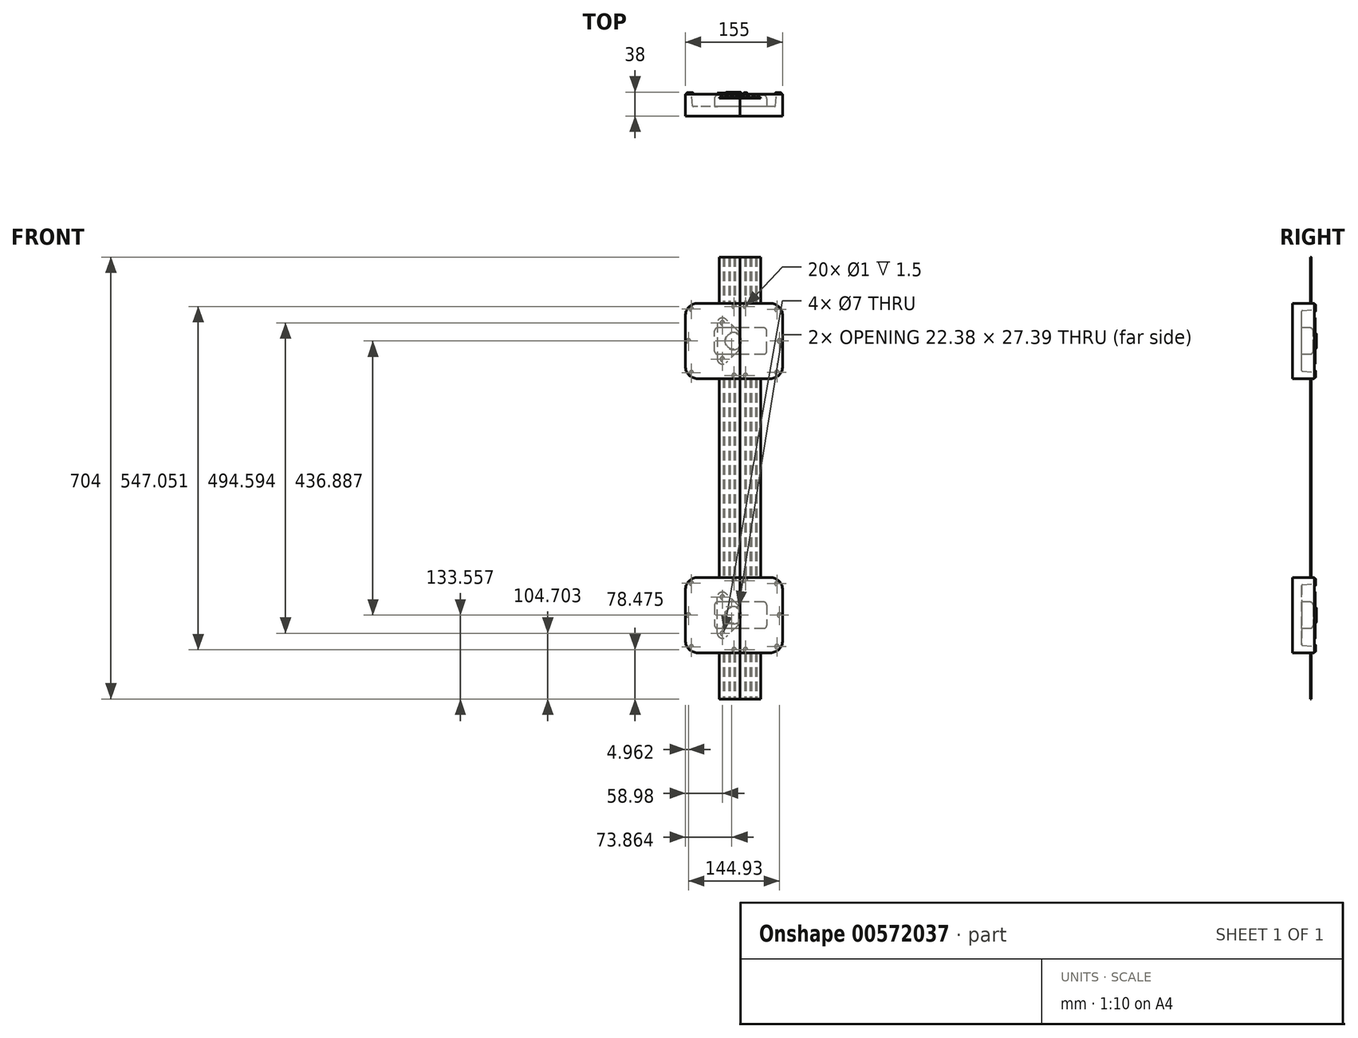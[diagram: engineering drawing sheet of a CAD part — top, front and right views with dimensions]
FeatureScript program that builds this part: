
annotation { "Feature Type Name" : "Feature", "Feature Type Description" : "" }
export const myFeature = defineFeature(function(context is Context, id is Id, definition is map)
    precondition{}
    {
        {
            var Q0;
            Q0=qCreatedBy(makeId("Top.planeOp"),FACE);
            var sketch = newSketch(context, id + "F0", { "sketchPlane" : qUnion([Q0])});
            skLineSegment(sketch, "E0", {"start": v(0, 0) * mm, "end": v(0, 7.5) * mm});
            skPoint(sketch, "E1.visualSharp", {"position": v(0, 36) * mm});
            skArc(sketch, "E1.filletArc", {"start": v(0.59, 35.41) * mm, "mid": v(0.15, 34.77) * mm, "end": v(0, 34) * mm});
            skLineSegment(sketch, "E2.1", {"start": v(1.5, 0) * mm, "end": v(1.5, 33.5) * mm});
            skLineSegment(sketch, "E3", {"start": v(1.5, 0) * mm, "end": v(0, 0) * mm});
            skPoint(sketch, "E4.visualSharp", {"position": v(1.5, 34.5) * mm});
            skArc(sketch, "E4.filletArc", {"start": v(1.8, 34.2) * mm, "mid": v(1.58, 33.88) * mm, "end": v(1.5, 33.5) * mm});
            skLineSegment(sketch, "E5.bottom", {"start": v(0, 18) * mm, "end": v(0.25, 18) * mm});
            skLineSegment(sketch, "E5.top", {"start": v(0, 16) * mm, "end": v(0.25, 16) * mm});
            skLineSegment(sketch, "E5.right", {"start": v(0.25, 18) * mm, "end": v(0.25, 16) * mm});
            skPoint(sketch, "E5.middle", {"position": v(0, 17) * mm});
            skLineSegment(sketch, "E6", {"start": v(0, 0) * mm, "end": v(-1.84, 0) * mm, "construction": true});
            skLineSegment(sketch, "E7", {"start": v(-1.84, 0) * mm, "end": v(-1.84, 17) * mm, "construction": true});
            skPoint(sketch, "E7.endSnap0", {"position": v(-0.25, 17) * mm});
            skLineSegment(sketch, "E8", {"start": v(-1.84, 8.5) * mm, "end": v(0, 8.5) * mm, "construction": true});
            skLineSegment(sketch, "E9.bottom", {"start": v(0.25, 9.5) * mm, "end": v(0, 9.5) * mm});
            skLineSegment(sketch, "E9.top", {"start": v(0.25, 7.5) * mm, "end": v(0, 7.5) * mm});
            skLineSegment(sketch, "E9.left", {"start": v(0.25, 9.5) * mm, "end": v(0.25, 7.5) * mm});
            skPoint(sketch, "E9.middle", {"position": v(0, 8.5) * mm});
            skLineSegment(sketch, "E10", {"start": v(-1.84, 17) * mm, "end": v(-1.84, 34) * mm, "construction": true});
            skLineSegment(sketch, "E11", {"start": v(-1.84, 25.5) * mm, "end": v(0, 25.5) * mm, "construction": true});
            skLineSegment(sketch, "E12.bottom", {"start": v(0.25, 26.5) * mm, "end": v(0, 26.5) * mm});
            skLineSegment(sketch, "E12.top", {"start": v(0.25, 24.5) * mm, "end": v(0, 24.5) * mm});
            skLineSegment(sketch, "E12.left", {"start": v(0.25, 26.5) * mm, "end": v(0.25, 24.5) * mm});
            skPoint(sketch, "E12.middle", {"position": v(0, 25.5) * mm});
            skPoint(sketch, "E13.end.orphan", {"position": v(36, 36) * mm});
            skLineSegment(sketch, "E14.trimOffspring", {"start": v(0, 9.5) * mm, "end": v(0, 16) * mm});
            skPoint(sketch, "E15.orphan", {"position": v(-0.25, 9.5) * mm});
            skPoint(sketch, "E16.orphan", {"position": v(-0.25, 7.5) * mm});
            skPoint(sketch, "E17.orphan", {"position": v(-0.25, 16) * mm});
            skLineSegment(sketch, "E18.trimOffspring", {"start": v(0, 18) * mm, "end": v(0, 24.5) * mm});
            skPoint(sketch, "E19.orphan", {"position": v(-0.25, 18) * mm});
            skLineSegment(sketch, "E20.trimOffspring", {"start": v(0, 26.5) * mm, "end": v(0, 34) * mm});
            skPoint(sketch, "E21.orphan", {"position": v(-0.25, 24.5) * mm});
            skPoint(sketch, "E22.orphan", {"position": v(-0.25, 26.5) * mm});
            skLineSegment(sketch, "E23.MirrorCS", {"start": v(11.5, 35.75) * mm, "end": v(11.5, 36) * mm});
            skLineSegment(sketch, "E24.MirrorCS", {"start": v(26.5, 35.75) * mm, "end": v(28.5, 35.75) * mm});
            skLineSegment(sketch, "E25.MirrorCS", {"start": v(28.5, 35.75) * mm, "end": v(28.5, 36) * mm});
            skLineSegment(sketch, "E26.MirrorCS", {"start": v(9.5, 35.75) * mm, "end": v(11.5, 35.75) * mm});
            skLineSegment(sketch, "E27.MirrorCS", {"start": v(9.5, 35.75) * mm, "end": v(9.5, 36) * mm});
            skLineSegment(sketch, "E28.MirrorCS", {"start": v(20, 36) * mm, "end": v(20, 35.75) * mm});
            skLineSegment(sketch, "E29.MirrorCS", {"start": v(26.5, 35.75) * mm, "end": v(26.5, 36) * mm});
            skLineSegment(sketch, "E30.MirrorCS", {"start": v(18, 35.75) * mm, "end": v(20, 35.75) * mm});
            skLineSegment(sketch, "E31.MirrorCS", {"start": v(18, 36) * mm, "end": v(18, 35.75) * mm});
            skArc(sketch, "E32.MirrorCS", {"start": v(1.8, 34.2) * mm, "mid": v(2.12, 34.42) * mm, "end": v(2.5, 34.5) * mm});
            skLineSegment(sketch, "E33.MirrorCS", {"start": v(36, 34.5) * mm, "end": v(36, 36) * mm});
            skArc(sketch, "E34.MirrorCS", {"start": v(0.59, 35.41) * mm, "mid": v(1.23, 35.85) * mm, "end": v(2, 36) * mm});
            skLineSegment(sketch, "E35.MirrorCS", {"start": v(10.5, 37.84) * mm, "end": v(10.5, 36) * mm, "construction": true});
            skLineSegment(sketch, "E36.MirrorCS", {"start": v(36, 36) * mm, "end": v(36, 37.84) * mm, "construction": true});
            skPoint(sketch, "E37.MirrorP", {"position": v(19, 36.25) * mm});
            skLineSegment(sketch, "E38.MirrorCS", {"start": v(27.5, 37.84) * mm, "end": v(27.5, 36) * mm, "construction": true});
            skPoint(sketch, "E39.MirrorP", {"position": v(19, 36) * mm});
            skLineSegment(sketch, "E40.MirrorCS", {"start": v(36, 34.5) * mm, "end": v(2.5, 34.5) * mm});
            skPoint(sketch, "E41.MirrorP", {"position": v(27.5, 36) * mm});
            skLineSegment(sketch, "E42.MirrorCS", {"start": v(36, 36) * mm, "end": v(28.5, 36) * mm});
            skLineSegment(sketch, "E43.MirrorCS", {"start": v(19, 37.84) * mm, "end": v(2, 37.84) * mm, "construction": true});
            skPoint(sketch, "E44.MirrorP", {"position": v(28.5, 36.25) * mm});
            skLineSegment(sketch, "E45.MirrorCS", {"start": v(18, 36) * mm, "end": v(11.5, 36) * mm});
            skPoint(sketch, "E46.MirrorP", {"position": v(18, 36.25) * mm});
            skPoint(sketch, "E47.MirrorP", {"position": v(10.5, 36) * mm});
            skPoint(sketch, "E48.MirrorP", {"position": v(9.5, 36.25) * mm});
            skPoint(sketch, "E49.MirrorP", {"position": v(20, 36.25) * mm});
            skPoint(sketch, "E50.MirrorP", {"position": v(26.5, 36.25) * mm});
            skLineSegment(sketch, "E51.MirrorCS", {"start": v(9.5, 36) * mm, "end": v(2, 36) * mm});
            skLineSegment(sketch, "E52.MirrorCS", {"start": v(36, 37.84) * mm, "end": v(19, 37.84) * mm, "construction": true});
            skPoint(sketch, "E53.MirrorP", {"position": v(11.5, 36.25) * mm});
            skLineSegment(sketch, "E54.MirrorCS", {"start": v(26.5, 36) * mm, "end": v(20, 36) * mm});
            skSolve(sketch);
        }
        {
            var Q0;
            Q0=qSketchRegion(id+"F0",true);
            extrude(context, id + "F1", {"entities" : qUnion([Q0]), "depth" : 704 * mm, "offsetDistance" : 25 * mm});
        }
        {
            var Q0;
            Q0=makeQuery(id+"F1.opExtrude","CAP_FACE",FACE,{"disambiguationData":[OSD([sQuery(id+"F0.wireOp",EDGE,"E0"),sQuery(id+"F0.wireOp",EDGE,"E1.filletArc"),sQuery(id+"F0.wireOp",EDGE,"E2.1"),sQuery(id+"F0.wireOp",EDGE,"E3"),sQuery(id+"F0.wireOp",EDGE,"E4.filletArc"),sQuery(id+"F0.wireOp",EDGE,"E5.bottom"),sQuery(id+"F0.wireOp",EDGE,"E5.top"),sQuery(id+"F0.wireOp",EDGE,"E5.right"),sQuery(id+"F0.wireOp",EDGE,"E9.bottom"),sQuery(id+"F0.wireOp",EDGE,"E9.top"),sQuery(id+"F0.wireOp",EDGE,"E9.left"),sQuery(id+"F0.wireOp",EDGE,"E12.bottom"),sQuery(id+"F0.wireOp",EDGE,"E12.top"),sQuery(id+"F0.wireOp",EDGE,"E12.left"),sQuery(id+"F0.wireOp",EDGE,"E14.trimOffspring"),sQuery(id+"F0.wireOp",EDGE,"E18.trimOffspring"),sQuery(id+"F0.wireOp",EDGE,"E20.trimOffspring"),sQuery(id+"F0.wireOp",EDGE,"E23.MirrorCS"),sQuery(id+"F0.wireOp",EDGE,"E24.MirrorCS"),sQuery(id+"F0.wireOp",EDGE,"E25.MirrorCS"),sQuery(id+"F0.wireOp",EDGE,"E26.MirrorCS"),sQuery(id+"F0.wireOp",EDGE,"E27.MirrorCS"),sQuery(id+"F0.wireOp",EDGE,"E28.MirrorCS"),sQuery(id+"F0.wireOp",EDGE,"E29.MirrorCS"),sQuery(id+"F0.wireOp",EDGE,"E30.MirrorCS"),sQuery(id+"F0.wireOp",EDGE,"E31.MirrorCS"),sQuery(id+"F0.wireOp",EDGE,"E32.MirrorCS"),sQuery(id+"F0.wireOp",EDGE,"E33.MirrorCS"),sQuery(id+"F0.wireOp",EDGE,"E34.MirrorCS"),sQuery(id+"F0.wireOp",EDGE,"E40.MirrorCS"),sQuery(id+"F0.wireOp",EDGE,"E42.MirrorCS"),sQuery(id+"F0.wireOp",EDGE,"E45.MirrorCS"),sQuery(id+"F0.wireOp",EDGE,"E51.MirrorCS"),sQuery(id+"F0.wireOp",EDGE,"E54.MirrorCS")])],"isStart":false});
            var sketch = newSketch(context, id + "F2", { "sketchPlane" : qUnion([Q0])});
            skLineSegment(sketch, "E55.bottom", {"start": v(0, 0) * mm, "end": v(3, 0) * mm});
            skLineSegment(sketch, "E55.top", {"start": v(0, 37.06) * mm, "end": v(3, 37.06) * mm});
            skLineSegment(sketch, "E55.left", {"start": v(0, 0) * mm, "end": v(0, 37.06) * mm});
            skLineSegment(sketch, "E55.right", {"start": v(3, 0) * mm, "end": v(3, 37.06) * mm});
            skSolve(sketch);
        }
        {
            var Q0;
            {var subQ4=sQuery(id+"F2.wireOp",EDGE,"E55.top");Q0=makeQuery(id+"F2.imprint","IMPRINT",FACE,{"disambiguationData":[TD([[makeQuery(id+"F2.imprint","IMPRINT",EDGE,{"derivedFrom":subQ4}),-1.0]])]});}
            var Q1;
            {var subQ4=sQuery(id+"F0.wireOp",EDGE,"E2.1");Q1=makeQuery(id+"F2.imprint","IMPRINT",FACE,{"disambiguationData":[TD([[makeQuery(id+"F2.imprint","IMPRINT",EDGE,{"derivedFrom":makeQuery(id+"F1.opExtrude","CAP_EDGE",EDGE,{"disambiguationData":[OSD([subQ4])],"isStart":false})}),-1.0]])]});}
            var Q2;
            {var subQ13=sQuery(id+"F0.wireOp",EDGE,"E5.right");Q2=makeQuery(id+"F2.imprint","IMPRINT",FACE,{"disambiguationData":[TD([[makeQuery(id+"F2.imprint","IMPRINT",EDGE,{"derivedFrom":makeQuery(id+"F1.opExtrude","CAP_EDGE",EDGE,{"disambiguationData":[OSD([subQ13])],"isStart":false})}),1.0]])]});}
            extrude(context, id + "F3", {"entities" : qUnion([Q0, Q1, Q2]), "operationType" : NewBodyOperationType.REMOVE, "endBound" : BoundingType.THROUGH_ALL, "oppositeDirection" : true, "depth" : 25 * mm, "offsetDistance" : 25 * mm});
        }
        {
            var Q0;
            Q0=makeQuery(id+"F3.boolean.opBoolean","INTERSECT",EDGE,{"derivedFrom":[makeQuery(id+"F1.opExtrude","SWEPT_FACE",FACE,{"disambiguationData":[OSD([sQuery(id+"F0.wireOp",EDGE,"E51.MirrorCS")])]}),makeQuery(id+"F3.opExtrude","SWEPT_FACE",FACE,{"disambiguationData":[OSD([sQuery(id+"F2.wireOp",EDGE,"E55.right")])]})]});
            var Q1;
            Q1=makeQuery(id+"F1.opExtrude","SWEPT_EDGE",EDGE,{"disambiguationData":[OSD([sQuery(id+"F0.wireOp",EDGE,"E33.MirrorCS"),sQuery(id+"F0.wireOp",EDGE,"E42.MirrorCS")])]});
            fillet(context, id + "F4", {"entities" : qUnion([Q0, Q1]), "radius" : 2 * mm, "tangentPropagation" : true, "allowEdgeOverflow" : false});
        }
        {
            var Q0;
            Q0=makeQuery(id+"F1.opExtrude","SWEPT_EDGE",EDGE,{"disambiguationData":[OSD([sQuery(id+"F0.wireOp",EDGE,"E31.MirrorCS"),sQuery(id+"F0.wireOp",EDGE,"E45.MirrorCS")])]});
            var Q1;
            Q1=makeQuery(id+"F1.opExtrude","SWEPT_EDGE",EDGE,{"disambiguationData":[OSD([sQuery(id+"F0.wireOp",EDGE,"E28.MirrorCS"),sQuery(id+"F0.wireOp",EDGE,"E54.MirrorCS")])]});
            var Q2;
            Q2=makeQuery(id+"F1.opExtrude","SWEPT_EDGE",EDGE,{"disambiguationData":[OSD([sQuery(id+"F0.wireOp",EDGE,"E25.MirrorCS"),sQuery(id+"F0.wireOp",EDGE,"E42.MirrorCS")])]});
            var Q3;
            Q3=makeQuery(id+"F1.opExtrude","SWEPT_EDGE",EDGE,{"disambiguationData":[OSD([sQuery(id+"F0.wireOp",EDGE,"E29.MirrorCS"),sQuery(id+"F0.wireOp",EDGE,"E54.MirrorCS")])]});
            var Q4;
            Q4=makeQuery(id+"F1.opExtrude","SWEPT_EDGE",EDGE,{"disambiguationData":[OSD([sQuery(id+"F0.wireOp",EDGE,"E27.MirrorCS"),sQuery(id+"F0.wireOp",EDGE,"E51.MirrorCS")])]});
            var Q5;
            Q5=makeQuery(id+"F1.opExtrude","SWEPT_EDGE",EDGE,{"disambiguationData":[OSD([sQuery(id+"F0.wireOp",EDGE,"E23.MirrorCS"),sQuery(id+"F0.wireOp",EDGE,"E45.MirrorCS")])]});
            fillet(context, id + "F5", {"entities" : qUnion([Q0, Q1, Q2, Q3, Q4, Q5]), "radius" : 0.2 * mm, "tangentPropagation" : true, "allowEdgeOverflow" : false});
        }
        {
            var Q0;
            Q0=qCreatedBy(makeId("Right.planeOp"),FACE);
            cPlane(context, id + "F6", {"entities" : qUnion([Q0]), "cplaneType" : CPlaneType.OFFSET, "offset" : 36.1 * mm, "width" : 150 * mm, "height" : 150 * mm});
        }
        {
            var Q0;
            Q0=makeQuery(id+"F1.opExtrude","SWEPT_BODY",BODY,{"disambiguationData":[OSD([sQuery(id+"F0.wireOp",EDGE,"E0"),sQuery(id+"F0.wireOp",EDGE,"E1.filletArc"),sQuery(id+"F0.wireOp",EDGE,"E2.1"),sQuery(id+"F0.wireOp",EDGE,"E3"),sQuery(id+"F0.wireOp",EDGE,"E4.filletArc"),sQuery(id+"F0.wireOp",EDGE,"E5.bottom"),sQuery(id+"F0.wireOp",EDGE,"E5.top"),sQuery(id+"F0.wireOp",EDGE,"E5.right"),sQuery(id+"F0.wireOp",EDGE,"E9.bottom"),sQuery(id+"F0.wireOp",EDGE,"E9.top"),sQuery(id+"F0.wireOp",EDGE,"E9.left"),sQuery(id+"F0.wireOp",EDGE,"E12.bottom"),sQuery(id+"F0.wireOp",EDGE,"E12.top"),sQuery(id+"F0.wireOp",EDGE,"E12.left"),sQuery(id+"F0.wireOp",EDGE,"E14.trimOffspring"),sQuery(id+"F0.wireOp",EDGE,"E18.trimOffspring"),sQuery(id+"F0.wireOp",EDGE,"E20.trimOffspring"),sQuery(id+"F0.wireOp",EDGE,"E23.MirrorCS"),sQuery(id+"F0.wireOp",EDGE,"E24.MirrorCS"),sQuery(id+"F0.wireOp",EDGE,"E25.MirrorCS"),sQuery(id+"F0.wireOp",EDGE,"E26.MirrorCS"),sQuery(id+"F0.wireOp",EDGE,"E27.MirrorCS"),sQuery(id+"F0.wireOp",EDGE,"E28.MirrorCS"),sQuery(id+"F0.wireOp",EDGE,"E29.MirrorCS"),sQuery(id+"F0.wireOp",EDGE,"E30.MirrorCS"),sQuery(id+"F0.wireOp",EDGE,"E31.MirrorCS"),sQuery(id+"F0.wireOp",EDGE,"E32.MirrorCS"),sQuery(id+"F0.wireOp",EDGE,"E33.MirrorCS"),sQuery(id+"F0.wireOp",EDGE,"E34.MirrorCS"),sQuery(id+"F0.wireOp",EDGE,"E40.MirrorCS"),sQuery(id+"F0.wireOp",EDGE,"E42.MirrorCS"),sQuery(id+"F0.wireOp",EDGE,"E45.MirrorCS"),sQuery(id+"F0.wireOp",EDGE,"E51.MirrorCS"),sQuery(id+"F0.wireOp",EDGE,"E54.MirrorCS")])]});
            var Q1;
            Q1=qCreatedBy(id+"F6.planeOp",FACE);
            mirror(context, id + "F7", {"operationType" : NewBodyOperationType.ADD, "entities" : qUnion([Q0]), "mirrorPlane" : qUnion([Q1])});
        }
        {
            var Q0;
            Q0=makeQuery(id+"F7.opPattern","COPY",FACE,{"derivedFrom":makeQuery(id+"F1.opExtrude","SWEPT_FACE",FACE,{"disambiguationData":[OSD([sQuery(id+"F0.wireOp",EDGE,"E42.MirrorCS")])]}),"instanceName":"1"});
            var sketch = newSketch(context, id + "F8", { "sketchPlane" : qUnion([Q0])});
            skLineSegment(sketch, "E56.bottom", {"start": v(-94.76, 73.56) * mm, "end": v(55.24, 73.56) * mm});
            skLineSegment(sketch, "E56.top", {"start": v(-94.76, 193.56) * mm, "end": v(55.24, 193.56) * mm});
            skLineSegment(sketch, "E56.left", {"start": v(-94.76, 73.56) * mm, "end": v(-94.76, 193.56) * mm});
            skLineSegment(sketch, "E56.right", {"start": v(55.24, 73.56) * mm, "end": v(55.24, 193.56) * mm});
            skPoint(sketch, "E56.middle", {"position": v(-19.76, 133.56) * mm});
            skLineSegment(sketch, "E57", {"start": v(32.68, 352) * mm, "end": v(-137.04, 352) * mm, "construction": true});
            skPoint(sketch, "E57.startSnap0", {"position": v(-43.5, 352) * mm});
            skLineSegment(sketch, "E58.MirrorCS", {"start": v(-94.76, 510.44) * mm, "end": v(55.24, 510.44) * mm});
            skPoint(sketch, "E59.MirrorP", {"position": v(-19.76, 570.44) * mm});
            skLineSegment(sketch, "E60.MirrorCS", {"start": v(-94.76, 630.44) * mm, "end": v(55.24, 630.44) * mm});
            skLineSegment(sketch, "E61.MirrorCS", {"start": v(-94.76, 630.44) * mm, "end": v(-94.76, 510.44) * mm});
            skLineSegment(sketch, "E62.MirrorCS", {"start": v(55.24, 630.44) * mm, "end": v(55.24, 510.44) * mm});
            skSolve(sketch);
        }
        {
            var Q0;
            Q0 = qSketchRegion(id + "F8", true);
            extrude(context, id + "F9", {"entities" : qUnion([Q0]), "operationType" : NewBodyOperationType.REMOVE, "oppositeDirection" : true, "depth" : 25 * mm, "offsetDistance" : 25 * mm, "hasSecondDirection" : true, "secondDirectionOppositeDirection" : false, "secondDirectionDepth" : 25 * mm});
        }
        {
            var Q0;
            {var subQ0=sQuery(id+"F0.wireOp",EDGE,"E51.MirrorCS");Q0=makeQuery(id+"F9.boolean.opBoolean","SPLIT",FACE,{"disambiguationData":[TD([makeQuery(id+"F9.opExtrude","SWEPT_FACE",FACE,{"disambiguationData":[OSD([sQuery(id+"F8.wireOp",EDGE,"E56.bottom")])]})])],"derivedFrom":makeQuery(id+"F7.opPattern","COPY",FACE,{"derivedFrom":makeQuery(id+"F1.opExtrude","SWEPT_FACE",FACE,{"disambiguationData":[OSD([subQ0])]}),"instanceName":"1"})});}
            var sketch = newSketch(context, id + "F10", { "sketchPlane" : qUnion([Q0])});
            skLineSegment(sketch, "E63.bottom", {"start": v(-84.02, 73.56) * mm, "end": v(30.98, 73.56) * mm});
            skLineSegment(sketch, "E63.top", {"start": v(-84.02, 193.56) * mm, "end": v(30.98, 193.56) * mm});
            skLineSegment(sketch, "E63.left", {"start": v(-104.02, 93.56) * mm, "end": v(-104.02, 173.56) * mm});
            skLineSegment(sketch, "E63.right", {"start": v(50.98, 93.56) * mm, "end": v(50.98, 173.56) * mm});
            skPoint(sketch, "E64.visualSharp", {"position": v(-104.02, 73.56) * mm});
            skArc(sketch, "E64.filletArc", {"start": v(-104.02, 93.56) * mm, "mid": v(-98.16, 79.41) * mm, "end": v(-84.02, 73.56) * mm});
            skPoint(sketch, "E65.visualSharp", {"position": v(-104.02, 193.56) * mm});
            skArc(sketch, "E65.filletArc", {"start": v(-84.02, 193.56) * mm, "mid": v(-98.16, 187.7) * mm, "end": v(-104.02, 173.56) * mm});
            skPoint(sketch, "E66.visualSharp", {"position": v(50.98, 193.56) * mm});
            skArc(sketch, "E66.filletArc", {"start": v(50.98, 173.56) * mm, "mid": v(45.13, 187.7) * mm, "end": v(30.98, 193.56) * mm});
            skPoint(sketch, "E67.visualSharp", {"position": v(50.98, 73.56) * mm});
            skArc(sketch, "E67.filletArc", {"start": v(30.98, 73.56) * mm, "mid": v(45.13, 79.41) * mm, "end": v(50.98, 93.56) * mm});
            skSolve(sketch);
        }
        {
            var Q0;
            Q0 = qSketchRegion(id + "F10", true);
            extrude(context, id + "F11", {"entities" : qUnion([Q0]), "depth" : 5 * mm, "offsetDistance" : 25 * mm, "hasSecondDirection" : true, "secondDirectionOppositeDirection" : true, "secondDirectionDepth" : 30 * mm});
        }
        {
            var Q0;
            Q0=makeQuery(id+"F11.opExtrude","CAP_FACE",FACE,{"disambiguationData":[OSD([sQuery(id+"F10.wireOp",EDGE,"E63.bottom"),sQuery(id+"F10.wireOp",EDGE,"E63.top"),sQuery(id+"F10.wireOp",EDGE,"E63.left"),sQuery(id+"F10.wireOp",EDGE,"E63.right"),sQuery(id+"F10.wireOp",EDGE,"E64.filletArc"),sQuery(id+"F10.wireOp",EDGE,"E65.filletArc"),sQuery(id+"F10.wireOp",EDGE,"E66.filletArc"),sQuery(id+"F10.wireOp",EDGE,"E67.filletArc")])],"isStart":false});
            var sketch = newSketch(context, id + "F12", { "sketchPlane" : qUnion([Q0])});
            skLineSegment(sketch, "E68.0", {"start": v(-94.02, 173.56) * mm, "end": v(-94.02, 93.56) * mm});
            skArc(sketch, "E68.1", {"start": v(-84.02, 183.56) * mm, "mid": v(-91.09, 180.63) * mm, "end": v(-94.02, 173.56) * mm});
            skArc(sketch, "E68.2", {"start": v(-94.02, 93.56) * mm, "mid": v(-91.09, 86.49) * mm, "end": v(-84.02, 83.56) * mm});
            skLineSegment(sketch, "E68.3", {"start": v(30.98, 183.56) * mm, "end": v(-84.02, 183.56) * mm});
            skLineSegment(sketch, "E68.4", {"start": v(-84.02, 83.56) * mm, "end": v(30.98, 83.56) * mm});
            skArc(sketch, "E68.5", {"start": v(30.98, 83.56) * mm, "mid": v(38.05, 86.49) * mm, "end": v(40.98, 93.56) * mm});
            skLineSegment(sketch, "E68.6", {"start": v(40.98, 93.56) * mm, "end": v(40.98, 173.56) * mm});
            skArc(sketch, "E68.7", {"start": v(40.98, 173.56) * mm, "mid": v(38.05, 180.63) * mm, "end": v(30.98, 183.56) * mm});
            skSolve(sketch);
        }
        {
            var Q0;
            Q0 = qSketchRegion(id + "F12", true);
            extrude(context, id + "F13", {"entities" : qUnion([Q0]), "operationType" : NewBodyOperationType.REMOVE, "oppositeDirection" : true, "depth" : 20 * mm, "offsetDistance" : 25 * mm, "hasDraft" : true, "draftAngle" : 5 * degree, "draftPullDirection" : true});
        }
        {
            var Q0;
            Q0=makeQuery(id+"F11.opExtrude","CAP_FACE",FACE,{"disambiguationData":[OSD([sQuery(id+"F10.wireOp",EDGE,"E63.bottom"),sQuery(id+"F10.wireOp",EDGE,"E63.top"),sQuery(id+"F10.wireOp",EDGE,"E63.left"),sQuery(id+"F10.wireOp",EDGE,"E63.right"),sQuery(id+"F10.wireOp",EDGE,"E64.filletArc"),sQuery(id+"F10.wireOp",EDGE,"E65.filletArc"),sQuery(id+"F10.wireOp",EDGE,"E66.filletArc"),sQuery(id+"F10.wireOp",EDGE,"E67.filletArc")])],"isStart":false});
            var Q1;
            Q1=makeQuery(id+"F13.boolean.opBoolean","COPY",FACE,{"derivedFrom":makeQuery(id+"F13.opExtrude","CAP_FACE",FACE,{"disambiguationData":[OSD([sQuery(id+"F12.wireOp",EDGE,"E68.0"),sQuery(id+"F12.wireOp",EDGE,"E68.1"),sQuery(id+"F12.wireOp",EDGE,"E68.2"),sQuery(id+"F12.wireOp",EDGE,"E68.3"),sQuery(id+"F12.wireOp",EDGE,"E68.4"),sQuery(id+"F12.wireOp",EDGE,"E68.5"),sQuery(id+"F12.wireOp",EDGE,"E68.6"),sQuery(id+"F12.wireOp",EDGE,"E68.7")])],"isStart":false})});
            fillet(context, id + "F14", {"entities" : qUnion([Q0, Q1]), "radius" : 1 * mm, "tangentPropagation" : true, "allowEdgeOverflow" : false});
        }
        {
            var Q0;
            Q0=makeQuery(id+"F11.opExtrude","CAP_FACE",FACE,{"disambiguationData":[OSD([sQuery(id+"F10.wireOp",EDGE,"E63.bottom"),sQuery(id+"F10.wireOp",EDGE,"E63.top"),sQuery(id+"F10.wireOp",EDGE,"E63.left"),sQuery(id+"F10.wireOp",EDGE,"E63.right"),sQuery(id+"F10.wireOp",EDGE,"E64.filletArc"),sQuery(id+"F10.wireOp",EDGE,"E65.filletArc"),sQuery(id+"F10.wireOp",EDGE,"E66.filletArc"),sQuery(id+"F10.wireOp",EDGE,"E67.filletArc")])],"isStart":false});
            var sketch = newSketch(context, id + "F15", { "sketchPlane" : qUnion([Q0])});
            skCircle(sketch, "E69", {"center": v(-98.91, 133.56) * mm, "radius": 3.5 * mm});
            skCircle(sketch, "E70", {"center": v(-98.91, 133.56) * mm, "radius": 0.5 * mm});
            skCircle(sketch, "E71", {"center": v(-94.92, 83.43) * mm, "radius": 3.5 * mm});
            skCircle(sketch, "E72", {"center": v(-94.92, 83.43) * mm, "radius": 0.5 * mm});
            skCircle(sketch, "E73", {"center": v(-44.7, 78.47) * mm, "radius": 3.5 * mm});
            skCircle(sketch, "E74", {"center": v(-44.7, 78.47) * mm, "radius": 0.5 * mm});
            skCircle(sketch, "E75", {"center": v(46.02, 133.56) * mm, "radius": 3.5 * mm});
            skCircle(sketch, "E76", {"center": v(46.02, 133.56) * mm, "radius": 0.5 * mm});
            skCircle(sketch, "E77", {"center": v(41.31, 82.78) * mm, "radius": 3.5 * mm});
            skCircle(sketch, "E78", {"center": v(41.31, 82.78) * mm, "radius": 0.5 * mm});
            skCircle(sketch, "E79", {"center": v(-26.6, 78.55) * mm, "radius": 3.5 * mm});
            skCircle(sketch, "E80", {"center": v(-26.6, 78.55) * mm, "radius": 0.5 * mm});
            skLineSegment(sketch, "E81", {"start": v(139.82, 74.56) * mm, "end": v(139.82, 192.56) * mm, "construction": true});
            skLineSegment(sketch, "E82", {"start": v(-84.02, 74.56) * mm, "end": v(-84.02, 192.56) * mm, "construction": true});
            skLineSegment(sketch, "E83", {"start": v(-84.02, 133.56) * mm, "end": v(-101.6, 133.56) * mm, "construction": true});
            skPoint(sketch, "E83.endSnap0", {"position": v(-84.02, 133.56) * mm});
            skLineSegment(sketch, "E84", {"start": v(-84.02, 133.56) * mm, "end": v(54.57, 133.56) * mm, "construction": true});
            skCircle(sketch, "E85.MirrorC", {"center": v(-94.92, 183.68) * mm, "radius": 0.5 * mm});
            skCircle(sketch, "E86.MirrorC", {"center": v(-44.7, 188.64) * mm, "radius": 0.5 * mm});
            skCircle(sketch, "E87.MirrorC", {"center": v(-26.6, 188.56) * mm, "radius": 0.5 * mm});
            skCircle(sketch, "E88.MirrorC", {"center": v(41.31, 184.34) * mm, "radius": 0.5 * mm});
            skCircle(sketch, "E89.MirrorC", {"center": v(-44.7, 188.64) * mm, "radius": 3.5 * mm});
            skCircle(sketch, "E90.MirrorC", {"center": v(-94.92, 183.68) * mm, "radius": 3.5 * mm});
            skCircle(sketch, "E91.MirrorC", {"center": v(-26.6, 188.56) * mm, "radius": 3.5 * mm});
            skCircle(sketch, "E92.MirrorC", {"center": v(41.31, 184.34) * mm, "radius": 3.5 * mm});
            skSolve(sketch);
        }
        {
            var Q0;
            Q0 = qSketchRegion(id + "F15", true);
            extrude(context, id + "F16", {"entities" : qUnion([Q0]), "operationType" : NewBodyOperationType.ADD, "depth" : 2 * mm, "offsetDistance" : 25 * mm});
        }
        {
            var Q0;
            Q0=makeQuery(id+"F16.opExtrude","CAP_EDGE",EDGE,{"disambiguationData":[OSD([sQuery(id+"F15.wireOp",EDGE,"E77")])],"isStart":false});
            var Q1;
            Q1=makeQuery(id+"F16.opExtrude","CAP_EDGE",EDGE,{"disambiguationData":[OSD([sQuery(id+"F15.wireOp",EDGE,"E75")])],"isStart":false});
            var Q2;
            Q2=makeQuery(id+"F16.opExtrude","CAP_EDGE",EDGE,{"disambiguationData":[OSD([sQuery(id+"F15.wireOp",EDGE,"E92.MirrorC")])],"isStart":false});
            var Q3;
            Q3=makeQuery(id+"F16.opExtrude","CAP_EDGE",EDGE,{"disambiguationData":[OSD([sQuery(id+"F15.wireOp",EDGE,"E89.MirrorC")])],"isStart":false});
            var Q4;
            Q4=makeQuery(id+"F16.opExtrude","CAP_EDGE",EDGE,{"disambiguationData":[OSD([sQuery(id+"F15.wireOp",EDGE,"E90.MirrorC")])],"isStart":false});
            var Q5;
            Q5=makeQuery(id+"F16.opExtrude","CAP_EDGE",EDGE,{"disambiguationData":[OSD([sQuery(id+"F15.wireOp",EDGE,"E69")])],"isStart":false});
            var Q6;
            Q6=makeQuery(id+"F16.opExtrude","CAP_EDGE",EDGE,{"disambiguationData":[OSD([sQuery(id+"F15.wireOp",EDGE,"E71")])],"isStart":false});
            var Q7;
            Q7=makeQuery(id+"F16.opExtrude","CAP_EDGE",EDGE,{"disambiguationData":[OSD([sQuery(id+"F15.wireOp",EDGE,"E73")])],"isStart":false});
            var Q8;
            Q8=makeQuery(id+"F16.opExtrude","CAP_EDGE",EDGE,{"disambiguationData":[OSD([sQuery(id+"F15.wireOp",EDGE,"E79")])],"isStart":false});
            var Q9;
            Q9=makeQuery(id+"F16.opExtrude","CAP_EDGE",EDGE,{"disambiguationData":[OSD([sQuery(id+"F15.wireOp",EDGE,"E91.MirrorC")])],"isStart":false});
            fillet(context, id + "F17", {"entities" : qUnion([Q0, Q1, Q2, Q3, Q4, Q5, Q6, Q7, Q8, Q9]), "radius" : 1.5 * mm, "tangentPropagation" : true, "allowEdgeOverflow" : false});
        }
        {
            var Q0;
            Q0=makeQuery(id+"F16.opExtrude","CAP_EDGE",EDGE,{"disambiguationData":[OSD([sQuery(id+"F15.wireOp",EDGE,"E78")])],"isStart":false});
            var Q1;
            Q1=makeQuery(id+"F16.opExtrude","CAP_EDGE",EDGE,{"disambiguationData":[OSD([sQuery(id+"F15.wireOp",EDGE,"E76")])],"isStart":false});
            var Q2;
            Q2=makeQuery(id+"F16.opExtrude","CAP_EDGE",EDGE,{"disambiguationData":[OSD([sQuery(id+"F15.wireOp",EDGE,"E88.MirrorC")])],"isStart":false});
            var Q3;
            Q3=makeQuery(id+"F16.opExtrude","CAP_EDGE",EDGE,{"disambiguationData":[OSD([sQuery(id+"F15.wireOp",EDGE,"E86.MirrorC")])],"isStart":false});
            var Q4;
            Q4=makeQuery(id+"F16.opExtrude","CAP_EDGE",EDGE,{"disambiguationData":[OSD([sQuery(id+"F15.wireOp",EDGE,"E87.MirrorC")])],"isStart":false});
            var Q5;
            Q5=makeQuery(id+"F16.opExtrude","CAP_EDGE",EDGE,{"disambiguationData":[OSD([sQuery(id+"F15.wireOp",EDGE,"E85.MirrorC")])],"isStart":false});
            var Q6;
            Q6=makeQuery(id+"F16.opExtrude","CAP_EDGE",EDGE,{"disambiguationData":[OSD([sQuery(id+"F15.wireOp",EDGE,"E70")])],"isStart":false});
            var Q7;
            Q7=makeQuery(id+"F16.opExtrude","CAP_EDGE",EDGE,{"disambiguationData":[OSD([sQuery(id+"F15.wireOp",EDGE,"E72")])],"isStart":false});
            var Q8;
            Q8=makeQuery(id+"F16.opExtrude","CAP_EDGE",EDGE,{"disambiguationData":[OSD([sQuery(id+"F15.wireOp",EDGE,"E74")])],"isStart":false});
            var Q9;
            Q9=makeQuery(id+"F16.opExtrude","CAP_EDGE",EDGE,{"disambiguationData":[OSD([sQuery(id+"F15.wireOp",EDGE,"E80")])],"isStart":false});
            fillet(context, id + "F18", {"entities" : qUnion([Q0, Q1, Q2, Q3, Q4, Q5, Q6, Q7, Q8, Q9]), "radius" : 0.5 * mm, "tangentPropagation" : true, "allowEdgeOverflow" : false});
        }
        {
            var Q0;
            {var subQ6=sQuery(id+"F10.wireOp",EDGE,"E63.right");var subQ7=sQuery(id+"F10.wireOp",EDGE,"E63.left");var subQ8=sQuery(id+"F10.wireOp",EDGE,"E63.top");var subQ9=sQuery(id+"F10.wireOp",EDGE,"E63.bottom");var subQ10=sQuery(id+"F10.wireOp",EDGE,"E64.filletArc");var subQ11=sQuery(id+"F10.wireOp",EDGE,"E65.filletArc");var subQ12=sQuery(id+"F10.wireOp",EDGE,"E66.filletArc");var subQ13=sQuery(id+"F10.wireOp",EDGE,"E67.filletArc");Q0=makeQuery(id+"F16.boolean.opBoolean","SPLIT",FACE,{"disambiguationData":[TD([makeQuery(id+"F14.opFillet","BLEND_FACE",FACE,{"disambiguationData":[OSD([subQ9])]})])],"derivedFrom":makeQuery(id+"F11.opExtrude","CAP_FACE",FACE,{"disambiguationData":[OSD([subQ9,subQ8,subQ7,subQ6,subQ10,subQ11,subQ12,subQ13])],"isStart":false})});}
            var sketch = newSketch(context, id + "F19", { "sketchPlane" : qUnion([Q0])});
            skLineSegment(sketch, "E93.bottom", {"start": v(-36.2, 193.61) * mm, "end": v(-36, 193.61) * mm});
            skLineSegment(sketch, "E93.top", {"start": v(-36.2, 72.83) * mm, "end": v(-36, 72.83) * mm});
            skLineSegment(sketch, "E93.left", {"start": v(-36.2, 193.61) * mm, "end": v(-36.2, 72.83) * mm});
            skLineSegment(sketch, "E93.right", {"start": v(-36, 193.61) * mm, "end": v(-36, 72.83) * mm});
            skSolve(sketch);
        }
        {
            var Q0;
            Q0 = qSketchRegion(id + "F19", true);
            extrude(context, id + "F20", {"entities" : qUnion([Q0]), "operationType" : NewBodyOperationType.REMOVE, "endBound" : BoundingType.THROUGH_ALL, "oppositeDirection" : true, "depth" : 25 * mm, "offsetDistance" : 25 * mm});
        }
        {
            var Q0;
            {var subQ0=sQuery(id+"F10.wireOp",EDGE,"E63.bottom");var subQ2=sQuery(id+"F19.wireOp",EDGE,"E93.left");Q0=makeQuery(id+"F20.boolean.opBoolean","COPY",EDGE,{"disambiguationData":[TD([makeQuery(id+"F14.opFillet","BLEND_FACE",FACE,{"disambiguationData":[OSD([subQ0])]})])],"derivedFrom":makeQuery(id+"F20.opExtrude","CAP_EDGE",EDGE,{"disambiguationData":[OSD([subQ2])],"isStart":true})});}
            var Q1;
            {var subQ0=sQuery(id+"F10.wireOp",EDGE,"E63.bottom");var subQ1=sQuery(id+"F19.wireOp",EDGE,"E93.right");Q1=makeQuery(id+"F20.boolean.opBoolean","COPY",EDGE,{"disambiguationData":[TD([makeQuery(id+"F14.opFillet","BLEND_FACE",FACE,{"disambiguationData":[OSD([subQ0])]})])],"derivedFrom":makeQuery(id+"F20.opExtrude","CAP_EDGE",EDGE,{"disambiguationData":[OSD([subQ1])],"isStart":true})});}
            fillet(context, id + "F21", {"entities" : qUnion([Q0, Q1]), "radius" : 1 * mm, "tangentPropagation" : true, "allowEdgeOverflow" : false});
        }
        {
            var Q0;
            {var subQ0=sQuery(id+"F12.wireOp",EDGE,"E68.6");var subQ1=sQuery(id+"F12.wireOp",EDGE,"E68.5");var subQ2=sQuery(id+"F12.wireOp",EDGE,"E68.4");var subQ3=sQuery(id+"F12.wireOp",EDGE,"E68.3");var subQ4=sQuery(id+"F12.wireOp",EDGE,"E68.7");Q0=makeQuery(id+"F20.boolean.opBoolean","SPLIT",FACE,{"disambiguationData":[TD([makeQuery(id+"F20.opExtrude","SWEPT_FACE",FACE,{"disambiguationData":[OSD([sQuery(id+"F19.wireOp",EDGE,"E93.right")])]})])],"derivedFrom":makeQuery(id+"F13.boolean.opBoolean","COPY",FACE,{"derivedFrom":makeQuery(id+"F13.opExtrude","CAP_FACE",FACE,{"disambiguationData":[OSD([sQuery(id+"F12.wireOp",EDGE,"E68.0"),sQuery(id+"F12.wireOp",EDGE,"E68.1"),sQuery(id+"F12.wireOp",EDGE,"E68.2"),subQ3,subQ2,subQ1,subQ0,subQ4])],"isStart":false})})});}
            var sketch = newSketch(context, id + "F22", { "sketchPlane" : qUnion([Q0])});
            skLineSegment(sketch, "E94.bottom", {"start": v(-78.65, 154.61) * mm, "end": v(4.4, 154.61) * mm});
            skLineSegment(sketch, "E94.top", {"start": v(-78.65, 112.5) * mm, "end": v(4.4, 112.5) * mm});
            skLineSegment(sketch, "E94.left", {"start": v(-78.65, 154.61) * mm, "end": v(-78.65, 112.5) * mm});
            skLineSegment(sketch, "E94.right", {"start": v(4.4, 154.61) * mm, "end": v(4.4, 112.5) * mm});
            skPoint(sketch, "E94.middle", {"position": v(-37.13, 133.56) * mm});
            skPoint(sketch, "E94.middle.positionSnap0", {"position": v(-35, 133.56) * mm});
            skPoint(sketch, "E94.centerSnap0", {"position": v(-35, 133.56) * mm});
            skSolve(sketch);
        }
        {
            var Q0;
            Q0 = qSketchRegion(id + "F22", true);
            extrude(context, id + "F23", {"entities" : qUnion([Q0]), "depth" : 18 * mm, "offsetDistance" : 25 * mm});
        }
        {
            var Q0;
            Q0=makeQuery(id+"F23.opExtrude","SWEPT_EDGE",EDGE,{"disambiguationData":[OSD([sQuery(id+"F22.wireOp",EDGE,"E94.top"),sQuery(id+"F22.wireOp",EDGE,"E94.left")])]});
            var Q1;
            Q1=makeQuery(id+"F23.opExtrude","SWEPT_EDGE",EDGE,{"disambiguationData":[OSD([sQuery(id+"F22.wireOp",EDGE,"E94.bottom"),sQuery(id+"F22.wireOp",EDGE,"E94.left")])]});
            var Q2;
            Q2=makeQuery(id+"F23.opExtrude","SWEPT_EDGE",EDGE,{"disambiguationData":[OSD([sQuery(id+"F22.wireOp",EDGE,"E94.top"),sQuery(id+"F22.wireOp",EDGE,"E94.right")])]});
            var Q3;
            Q3=makeQuery(id+"F23.opExtrude","SWEPT_EDGE",EDGE,{"disambiguationData":[OSD([sQuery(id+"F22.wireOp",EDGE,"E94.bottom"),sQuery(id+"F22.wireOp",EDGE,"E94.right")])]});
            fillet(context, id + "F24", {"entities" : qUnion([Q0, Q1, Q2, Q3]), "radius" : 5 * mm, "tangentPropagation" : true, "allowEdgeOverflow" : false});
        }
        {
            var Q0;
            Q0=makeQuery(id+"F23.opExtrude","CAP_FACE",FACE,{"disambiguationData":[OSD([sQuery(id+"F22.wireOp",EDGE,"E94.bottom"),sQuery(id+"F22.wireOp",EDGE,"E94.top"),sQuery(id+"F22.wireOp",EDGE,"E94.left"),sQuery(id+"F22.wireOp",EDGE,"E94.right")])],"isStart":false});
            var sketch = newSketch(context, id + "F25", { "sketchPlane" : qUnion([Q0])});
            skCircle(sketch, "E95", {"center": v(-25.48, 133.56) * mm, "radius": 12.78 * mm});
            skPoint(sketch, "E95.centerSnap0", {"position": v(4.4, 133.56) * mm});
            skSolve(sketch);
        }
        {
            var Q0;
            Q0 = qSketchRegion(id + "F25", true);
            extrude(context, id + "F26", {"entities" : qUnion([Q0]), "operationType" : NewBodyOperationType.ADD, "depth" : 5 * mm, "offsetDistance" : 25 * mm});
        }
        {
            var Q0;
            Q0=makeQuery(id+"F23.opExtrude","CAP_EDGE",EDGE,{"disambiguationData":[OSD([sQuery(id+"F22.wireOp",EDGE,"E94.left")])],"isStart":false});
            fillet(context, id + "F27", {"entities" : qUnion([Q0]), "radius" : 5 * mm, "tangentPropagation" : true, "allowEdgeOverflow" : false});
        }
        {
            var Q0;
            Q0=makeQuery(id+"F26.opExtrude","CAP_EDGE",EDGE,{"disambiguationData":[OSD([sQuery(id+"F25.wireOp",EDGE,"E95")])],"isStart":false});
            fillet(context, id + "F28", {"entities" : qUnion([Q0]), "radius" : 2 * mm, "tangentPropagation" : true, "allowEdgeOverflow" : false});
        }
        {
            var Q0;
            Q0=makeQuery(id+"F23.opExtrude","CAP_FACE",FACE,{"disambiguationData":[OSD([sQuery(id+"F22.wireOp",EDGE,"E94.bottom"),sQuery(id+"F22.wireOp",EDGE,"E94.top"),sQuery(id+"F22.wireOp",EDGE,"E94.left"),sQuery(id+"F22.wireOp",EDGE,"E94.right")])],"isStart":false});
            cPlane(context, id + "F29", {"entities" : qUnion([Q0]), "cplaneType" : CPlaneType.OFFSET, "offset" : 2 * mm, "width" : 150 * mm, "height" : 150 * mm});
        }
        {
            var Q0;
            Q0=qCreatedBy(id+"F29.planeOp",FACE);
            var sketch = newSketch(context, id + "F30", { "sketchPlane" : qUnion([Q0])});
            skLineSegment(sketch, "E96", {"start": v(-35.05, 133.56) * mm, "end": v(-35.08, 144.04) * mm});
            skLineSegment(sketch, "E97", {"start": v(-32.62, 149.83) * mm, "end": v(-13.55, 168.18) * mm});
            skLineSegment(sketch, "E98", {"start": v(0, 162.41) * mm, "end": v(0, 133.56) * mm});
            skPoint(sketch, "E99.visualSharp", {"position": v(-35.09, 147.46) * mm});
            skArc(sketch, "E99.filletArc", {"start": v(-32.62, 149.83) * mm, "mid": v(-34.44, 147.18) * mm, "end": v(-35.08, 144.04) * mm});
            skPoint(sketch, "E100.visualSharp", {"position": v(0, 181.2) * mm});
            skArc(sketch, "E100.filletArc", {"start": v(0, 162.41) * mm, "mid": v(-4.87, 169.77) * mm, "end": v(-13.55, 168.18) * mm});
            skArc(sketch, "E101.0", {"start": v(-11.7, 133.56) * mm, "mid": v(-19.5, 145.97) * mm, "end": v(-34.07, 144.33) * mm});
            skLineSegment(sketch, "E102", {"start": v(3.18, 133.56) * mm, "end": v(-45.28, 133.56) * mm, "construction": true});
            skArc(sketch, "E103.MirrorCS", {"start": v(-32.62, 117.29) * mm, "mid": v(-34.44, 119.93) * mm, "end": v(-35.08, 123.07) * mm});
            skLineSegment(sketch, "E104.MirrorCS", {"start": v(0, 104.7) * mm, "end": v(0, 133.56) * mm});
            skPoint(sketch, "E105.MirrorP", {"position": v(-35.09, 119.66) * mm});
            skLineSegment(sketch, "E106.MirrorCS", {"start": v(-35.05, 133.56) * mm, "end": v(-35.08, 123.07) * mm});
            skArc(sketch, "E107.MirrorCS", {"start": v(0, 104.7) * mm, "mid": v(-4.87, 97.34) * mm, "end": v(-13.55, 98.94) * mm});
            skArc(sketch, "E108.MirrorCS", {"start": v(-11.7, 133.56) * mm, "mid": v(-19.5, 121.14) * mm, "end": v(-34.07, 122.79) * mm});
            skLineSegment(sketch, "E109.MirrorCS", {"start": v(-32.62, 117.29) * mm, "end": v(-13.55, 98.94) * mm});
            skPoint(sketch, "E110.1.end.orphan", {"position": v(-34.08, 144.04) * mm});
            skPoint(sketch, "E110.1.start.orphan", {"position": v(-34.05, 133.56) * mm});
            skPoint(sketch, "E111.MirrorCS.start.orphan", {"position": v(-34.05, 133.55) * mm});
            skPoint(sketch, "E112.MirrorCS.end.orphan", {"position": v(-34.08, 123.07) * mm});
            skLineSegment(sketch, "E113", {"start": v(-34.07, 122.79) * mm, "end": v(-34.07, 144.33) * mm});
            skCircle(sketch, "E114", {"center": v(-8, 104.7) * mm, "radius": 3.5 * mm});
            skCircle(sketch, "E115", {"center": v(-8, 162.41) * mm, "radius": 3.5 * mm});
            skSolve(sketch);
        }
        {
            var Q0;
            Q0 = qSketchRegion(id + "F30", true);
            extrude(context, id + "F31", {"entities" : qUnion([Q0]), "depth" : 1.5 * mm, "offsetDistance" : 25 * mm});
        }
        {
            var Q0;
            Q0=makeQuery(id+"F31.opExtrude","CAP_FACE",FACE,{"disambiguationData":[OSD([sQuery(id+"F30.wireOp",EDGE,"E96"),sQuery(id+"F30.wireOp",EDGE,"E97"),sQuery(id+"F30.wireOp",EDGE,"E98"),sQuery(id+"F30.wireOp",EDGE,"E99.filletArc"),sQuery(id+"F30.wireOp",EDGE,"E100.filletArc"),sQuery(id+"F30.wireOp",EDGE,"E101.0"),sQuery(id+"F30.wireOp",EDGE,"E103.MirrorCS"),sQuery(id+"F30.wireOp",EDGE,"E104.MirrorCS"),sQuery(id+"F30.wireOp",EDGE,"E106.MirrorCS"),sQuery(id+"F30.wireOp",EDGE,"E107.MirrorCS"),sQuery(id+"F30.wireOp",EDGE,"E108.MirrorCS"),sQuery(id+"F30.wireOp",EDGE,"E109.MirrorCS"),sQuery(id+"F30.wireOp",EDGE,"E113"),sQuery(id+"F30.wireOp",EDGE,"E114"),sQuery(id+"F30.wireOp",EDGE,"E115")])],"isStart":false});
            var Q1;
            {var subQ0=sQuery(id+"F0.wireOp",EDGE,"E51.MirrorCS");Q1=makeQuery(id+"F9.boolean.opBoolean","SPLIT",FACE,{"disambiguationData":[TD([makeQuery(id+"F9.opExtrude","SWEPT_FACE",FACE,{"disambiguationData":[OSD([sQuery(id+"F8.wireOp",EDGE,"E56.bottom")])]})])],"derivedFrom":makeQuery(id+"F1.opExtrude","SWEPT_FACE",FACE,{"disambiguationData":[OSD([subQ0])]})});}
            fillet(context, id + "F32", {"entities" : qUnion([Q0, Q1]), "radius" : 0.5 * mm, "tangentPropagation" : true, "allowEdgeOverflow" : false});
        }
        {
            var Q0;
            {var subQ0=sQuery(id+"F10.wireOp",EDGE,"E65.filletArc");var subQ1=sQuery(id+"F10.wireOp",EDGE,"E63.top");Q0=makeQuery(id+"F20.boolean.opBoolean","SPLIT",FACE,{"disambiguationData":[TD([makeQuery(id+"F11.opExtrude","SWEPT_FACE",FACE,{"disambiguationData":[OSD([subQ0])]})])],"derivedFrom":makeQuery(id+"F11.opExtrude","SWEPT_FACE",FACE,{"disambiguationData":[OSD([subQ1])]})});}
            var Q1;
            Q1=makeQuery(id+"F9.boolean.opBoolean","COPY",FACE,{"disambiguationData":[TD([makeQuery(id+"F7.opPattern","COPY",FACE,{"derivedFrom":makeQuery(id+"F1.opExtrude","SWEPT_FACE",FACE,{"disambiguationData":[OSD([sQuery(id+"F0.wireOp",EDGE,"E24.MirrorCS")])]}),"instanceName":"1"})])],"derivedFrom":makeQuery(id+"F9.opExtrude","SWEPT_FACE",FACE,{"disambiguationData":[OSD([sQuery(id+"F8.wireOp",EDGE,"E58.MirrorCS")])]})});
            cPlane(context, id + "F33", {"entities" : qUnion([Q0, Q1]), "cplaneType" : CPlaneType.MID_PLANE, "offset" : 25 * mm, "width" : 150 * mm, "height" : 150 * mm});
        }
        {
            var Q0;
            Q0=makeQuery(id+"F31.opExtrude","SWEPT_BODY",BODY,{"disambiguationData":[OSD([sQuery(id+"F30.wireOp",EDGE,"E96"),sQuery(id+"F30.wireOp",EDGE,"E97"),sQuery(id+"F30.wireOp",EDGE,"E98"),sQuery(id+"F30.wireOp",EDGE,"E99.filletArc"),sQuery(id+"F30.wireOp",EDGE,"E100.filletArc"),sQuery(id+"F30.wireOp",EDGE,"E101.0"),sQuery(id+"F30.wireOp",EDGE,"E103.MirrorCS"),sQuery(id+"F30.wireOp",EDGE,"E104.MirrorCS"),sQuery(id+"F30.wireOp",EDGE,"E106.MirrorCS"),sQuery(id+"F30.wireOp",EDGE,"E107.MirrorCS"),sQuery(id+"F30.wireOp",EDGE,"E108.MirrorCS"),sQuery(id+"F30.wireOp",EDGE,"E109.MirrorCS"),sQuery(id+"F30.wireOp",EDGE,"E113"),sQuery(id+"F30.wireOp",EDGE,"E114"),sQuery(id+"F30.wireOp",EDGE,"E115")])]});
            var Q1;
            Q1=makeQuery(id+"F20.boolean.opBoolean","SPLIT",BODY,{"disambiguationData":[OD(0.0)],"derivedFrom":makeQuery(id+"F11.opExtrude","SWEPT_BODY",BODY,{"disambiguationData":[OSD([sQuery(id+"F10.wireOp",EDGE,"E63.bottom"),sQuery(id+"F10.wireOp",EDGE,"E63.top"),sQuery(id+"F10.wireOp",EDGE,"E63.left"),sQuery(id+"F10.wireOp",EDGE,"E63.right"),sQuery(id+"F10.wireOp",EDGE,"E64.filletArc"),sQuery(id+"F10.wireOp",EDGE,"E65.filletArc"),sQuery(id+"F10.wireOp",EDGE,"E66.filletArc"),sQuery(id+"F10.wireOp",EDGE,"E67.filletArc")])]})});
            var Q2;
            Q2=makeQuery(id+"F23.opExtrude","SWEPT_BODY",BODY,{"disambiguationData":[OSD([sQuery(id+"F22.wireOp",EDGE,"E94.bottom"),sQuery(id+"F22.wireOp",EDGE,"E94.top"),sQuery(id+"F22.wireOp",EDGE,"E94.left"),sQuery(id+"F22.wireOp",EDGE,"E94.right")])]});
            var Q3;
            Q3=makeQuery(id+"F20.boolean.opBoolean","SPLIT",BODY,{"disambiguationData":[OD(1.0)],"derivedFrom":makeQuery(id+"F11.opExtrude","SWEPT_BODY",BODY,{"disambiguationData":[OSD([sQuery(id+"F10.wireOp",EDGE,"E63.bottom"),sQuery(id+"F10.wireOp",EDGE,"E63.top"),sQuery(id+"F10.wireOp",EDGE,"E63.left"),sQuery(id+"F10.wireOp",EDGE,"E63.right"),sQuery(id+"F10.wireOp",EDGE,"E64.filletArc"),sQuery(id+"F10.wireOp",EDGE,"E65.filletArc"),sQuery(id+"F10.wireOp",EDGE,"E66.filletArc"),sQuery(id+"F10.wireOp",EDGE,"E67.filletArc")])]})});
            var Q4;
            Q4=qCreatedBy(id+"F33.planeOp",FACE);
            mirror(context, id + "F34", {"entities" : qUnion([Q0, Q1, Q2, Q3]), "mirrorPlane" : qUnion([Q4])});
        }
    });
